# Revit family: РИДАН_Счетчик горячей и холодной воды СГВ
name_source: partatom
category: Арматура трубопроводов
units: mm (PartAtom-declared; Revit-internal decimal feet)

## family parameters
Всегда вертикально = Да
На основе рабочей плоскости = Нет
Общий = Нет
При загрузке вырезать с полостями = Нет
Размер круглого соединителя = Использовать диаметр
Тип детали = Вставляется

## types (18) — shared parameters
ADSK_Версия Revit = 2019
ADSK_Версия семейства = 1.0
ADSK_Единица измерения = шт.
ADSK_Завод-изготовитель = ООО «Ридан-Трейд»
ADSK_Количество = 1
ADSK_Расход жидкости = 0 м³/ч
LT = Table
URL = https://ridan.ru
j1 = 5 мм
Изготовитель = ООО «Ридан-Трейд»

## per-type parameters (varying)
| type | ADSK_Диаметр условный | ADSK_Код изделия | ADSK_Марка | ADSK_Масса | ADSK_Наименование | DN | a | b | c | d | e | f | g | h | i | i1 | j | k | num | Фитинги |
| СГВ-15ЭВ RS-485 (L80) С фитингами | 15 мм | 187F2045R | СГВ-15ЭВ | 0.35 | Счётчик воды СГВ-15ЭВ RS-485 Ридан (L80) С фитингами | 15 мм | 1 мм | 6 мм | 3 мм | 59 мм | 30 мм | 12 мм | 13 мм | 7 мм | 27 мм | 27 мм | 30 мм | 134 мм | 1 | Да |
| СГВ-15ЭВ RS-485 С фитингами | 15 мм | 187F2046R | СГВ-15ЭВ | 0.44 | Счётчик воды СГВ-15ЭВ RS-485 Ридан С фитингами | 15 мм | 1 мм | 6 мм | 3 мм | 89 мм | 45 мм | 12 мм | 13 мм | 7 мм | 27 мм | 27 мм | 30 мм | 164 мм | 2 | Да |
| СГВ-20ЭВ RS-485 С фитингами | 20 мм | 187F2047R | СГВ-20ЭВ | 0.48 | Счётчик воды СГВ-20ЭВ RS-485 Ридан С фитингами | 20 мм | 2 мм | 7 мм | 4 мм | 104 мм | 52 мм | 15 мм | 17 мм | 9 мм | 30 мм | 30 мм | 37 мм | 190 мм | 3 | Да |
| СГВ-15ЭВ RS-485 (L80) Без фитингов | 15 мм | 187F2048R | СГВ-15ЭВ | 0.29 | Счётчик воды СГВ-15ЭВ RS-485 Ридан (L80) Без фитингов | 20 мм | 1 мм | 6 мм | 3 мм | 59 мм | 30 мм | 12 мм | 13 мм | 7 мм | 27 мм | 0 мм | 30 мм | 80 мм | 4 | Нет |
| СГВ-15ЭВ RS-485 Без фитингов | 15 мм | 187F2049R | СГВ-15ЭВ | 0.54 | Счётчик воды СГВ-15ЭВ RS-485 Ридан Без фитингов | 20 мм | 1 мм | 6 мм | 3 мм | 89 мм | 45 мм | 12 мм | 13 мм | 7 мм | 27 мм | 0 мм | 30 мм | 110 мм | 5 | Нет |
| СГВ-20ЭВ RS-485 Без фитингов | 20 мм | 187F2050R | СГВ-20ЭВ | 0.4 | Счётчик воды СГВ-20ЭВ RS-485 Ридан Без фитингов | 25 мм | 2 мм | 7 мм | 4 мм | 104 мм | 52 мм | 15 мм | 17 мм | 9 мм | 30 мм | 0 мм | 37 мм | 130 мм | 6 | Нет |
| СГВ-15МВ c имп. вых. (L80) С фитингами | 15 мм | 187F2063R | СГВ-15МВ | 0.39 | Счётчик воды СГВ-15МВ c имп. вых. Ридан (L80) С фитингами | 15 мм | 1 мм | 6 мм | 3 мм | 59 мм | 30 мм | 12 мм | 13 мм | 7 мм | 27 мм | 27 мм | 30 мм | 134 мм | 7 | Да |
| СГВ-15МВ c имп. вых. С фитингами | 15 мм | 187F2064R | СГВ-15МВ | 0.35 | Счётчик воды СГВ-15МВ c имп. вых. Ридан С фитингами | 15 мм | 1 мм | 6 мм | 3 мм | 89 мм | 45 мм | 12 мм | 13 мм | 7 мм | 27 мм | 27 мм | 30 мм | 164 мм | 8 | Да |
| СГВ-20МВ c имп. вых. С фитингами | 20 мм | 187F2065R | СГВ-20МВ | 0.5 | Счётчик воды СГВ-20МВ c имп. вых. Ридан С фитингами | 20 мм | 2 мм | 7 мм | 4 мм | 104 мм | 52 мм | 15 мм | 17 мм | 9 мм | 30 мм | 30 мм | 37 мм | 190 мм | 9 | Да |
| СГВ-15МВ c имп. вых. (L80) Без фитингов | 15 мм | 187F2066R | СГВ-15МВ | 0.25 | Счётчик воды СГВ-15МВ c имп. вых. Ридан (L80) Без фитингов | 20 мм | 1 мм | 6 мм | 3 мм | 59 мм | 30 мм | 12 мм | 13 мм | 7 мм | 27 мм | 0 мм | 30 мм | 80 мм | 10 | Нет |
| СГВ-15МВ c имп. вых. Без фитингов | 15 мм | 187F2067R | СГВ-15МВ | 0.32 | Счётчик воды СГВ-15МВ c имп. вых. Ридан Без фитингов | 20 мм | 1 мм | 6 мм | 3 мм | 89 мм | 45 мм | 12 мм | 13 мм | 7 мм | 27 мм | 0 мм | 30 мм | 110 мм | 11 | Нет |
| СГВ-20МВ c имп. вых. Без фитингов | 20 мм | 187F2068R | СГВ-20МВ | 0.38 | Счётчик воды СГВ-20МВ c имп. вых. Ридан Без фитингов | 25 мм | 2 мм | 7 мм | 4 мм | 104 мм | 52 мм | 15 мм | 17 мм | 9 мм | 30 мм | 0 мм | 37 мм | 130 мм | 12 | Нет |
| СГВ-15МВ (L80) С фитингами | 15 мм | 187F2069R | СГВ-15МВ | 0.38 | Счётчик воды СГВ-15МВ Ридан (L80) С фитингами | 15 мм | 1 мм | 6 мм | 3 мм | 59 мм | 30 мм | 12 мм | 13 мм | 7 мм | 27 мм | 27 мм | 30 мм | 134 мм | 13 | Да |
| СГВ-15МВ С фитингами | 15 мм | 187F2070R | СГВ-15МВ | 0.42 | Счётчик воды СГВ-15МВ Ридан С фитингами | 15 мм | 1 мм | 6 мм | 3 мм | 89 мм | 45 мм | 12 мм | 13 мм | 7 мм | 27 мм | 27 мм | 30 мм | 164 мм | 14 | Да |
| СГВ-20МВ С фитингами | 20 мм | 187F2071R | СГВ-20МВ | 0.46 | Счётчик воды СГВ-20МВ Ридан С фитингами | 20 мм | 2 мм | 7 мм | 4 мм | 104 мм | 52 мм | 15 мм | 17 мм | 9 мм | 30 мм | 30 мм | 37 мм | 190 мм | 15 | Да |
| СГВ-15МВ (L80) Без фитингов | 15 мм | 187F2072R | СГВ-15МВ | 0.28 | Счётчик воды СГВ-15МВ Ридан (L80) Без фитингов | 20 мм | 1 мм | 6 мм | 3 мм | 59 мм | 30 мм | 12 мм | 13 мм | 7 мм | 27 мм | 0 мм | 30 мм | 80 мм | 16 | Нет |
| СГВ-15МВ Без фитингов | 15 мм | 187F2073R | СГВ-15МВ | 0.29 | Счётчик воды СГВ-15МВ Ридан Без фитингов | 20 мм | 1 мм | 6 мм | 3 мм | 89 мм | 45 мм | 12 мм | 13 мм | 7 мм | 27 мм | 0 мм | 30 мм | 110 мм | 17 | Нет |
| СГВ-20МВ Без фитингов | 20 мм | 187F2074R | СГВ-20МВ | 0.38 | Счётчик воды СГВ-20МВ Ридан Без фитингов | 25 мм | 2 мм | 7 мм | 4 мм | 104 мм | 52 мм | 15 мм | 17 мм | 9 мм | 30 мм | 0 мм | 37 мм | 130 мм | 18 | Нет |
